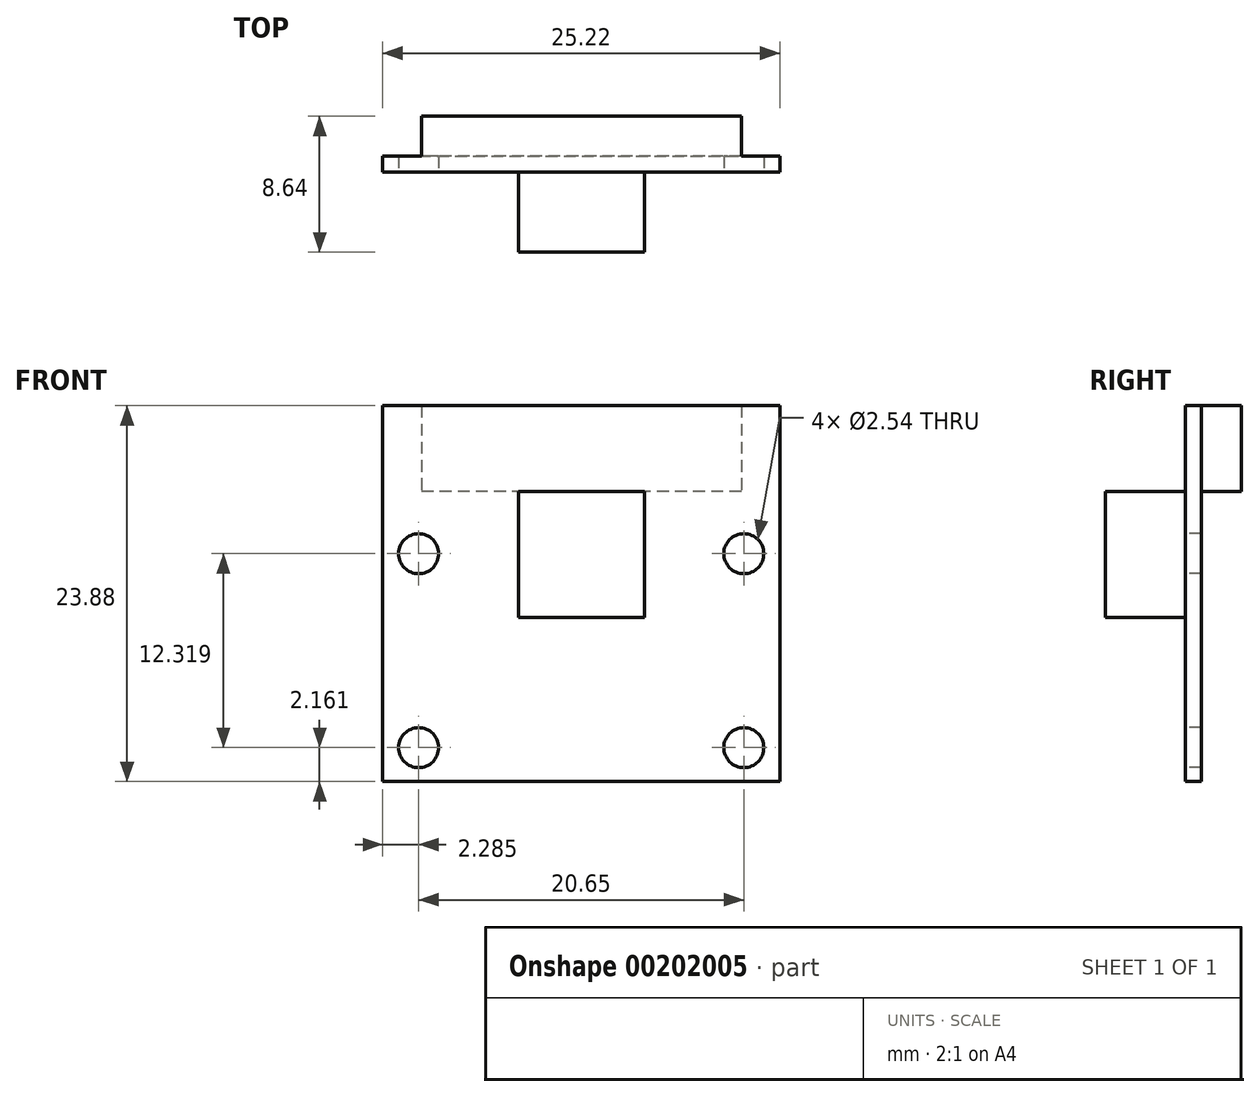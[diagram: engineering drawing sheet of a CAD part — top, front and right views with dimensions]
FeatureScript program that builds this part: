
annotation { "Feature Type Name" : "Feature", "Feature Type Description" : "" }
export const myFeature = defineFeature(function(context is Context, id is Id, definition is map)
    precondition{}
    {
        {
            var Q0;
            Q0=qCreatedBy(makeId("Front.planeOp"),FACE);
            var sketch = newSketch(context, id + "F0", { "sketchPlane" : qUnion([Q0])});
            skLineSegment(sketch, "E0.bottom", {"start": v(-12.61, 11.94) * mm, "end": v(12.61, 11.94) * mm});
            skLineSegment(sketch, "E0.top", {"start": v(-12.61, -11.94) * mm, "end": v(12.61, -11.94) * mm});
            skLineSegment(sketch, "E0.left", {"start": v(-12.61, 11.94) * mm, "end": v(-12.61, -11.94) * mm});
            skLineSegment(sketch, "E0.right", {"start": v(12.61, 11.94) * mm, "end": v(12.61, -11.94) * mm});
            skPoint(sketch, "E0.middle", {"position": v(0, 0) * mm});
            skCircle(sketch, "E1", {"center": v(10.33, -9.78) * mm, "radius": 1.27 * mm});
            skLineSegment(sketch, "E2", {"start": v(0, 11.94) * mm, "end": v(0, -11.94) * mm, "construction": true});
            skCircle(sketch, "E3", {"center": v(10.33, 2.54) * mm, "radius": 1.27 * mm});
            skCircle(sketch, "E4.MirrorC", {"center": v(-10.33, 2.54) * mm, "radius": 1.27 * mm});
            skCircle(sketch, "E5.MirrorC", {"center": v(-10.33, -9.78) * mm, "radius": 1.27 * mm});
            skSolve(sketch);
        }
        {
            var Q0;
            Q0=makeQuery(id+"F0.imprint","IMPRINT",FACE,{"disambiguationData":[TD([[makeQuery(id+"F0.imprint","IMPRINT",EDGE,{"derivedFrom":sQuery(id+"F0.wireOp",EDGE,"E0.bottom")}),-1.0]])]});
            extrude(context, id + "F1", {"entities" : qUnion([Q0]), "oppositeDirection" : true, "depth" : 1.02 * mm});
        }
        {
            var Q0;
            Q0=makeQuery(id+"F1.opExtrude","CAP_FACE",FACE,{"disambiguationData":[OSD([sQuery(id+"F0.wireOp",EDGE,"E0.bottom"),sQuery(id+"F0.wireOp",EDGE,"E0.top"),sQuery(id+"F0.wireOp",EDGE,"E0.left"),sQuery(id+"F0.wireOp",EDGE,"E0.right")])],"isStart":true});
            var sketch = newSketch(context, id + "F2", { "sketchPlane" : qUnion([Q0])});
            skLineSegment(sketch, "E6.bottom", {"start": v(-4, 6.48) * mm, "end": v(4, 6.48) * mm});
            skLineSegment(sketch, "E6.top", {"start": v(-4, -1.52) * mm, "end": v(4, -1.52) * mm});
            skLineSegment(sketch, "E6.left", {"start": v(-4, 6.48) * mm, "end": v(-4, -1.52) * mm});
            skLineSegment(sketch, "E6.right", {"start": v(4, 6.48) * mm, "end": v(4, -1.52) * mm});
            skPoint(sketch, "E6.middle", {"position": v(0, 2.48) * mm});
            skSolve(sketch);
        }
        {
            var Q0;
            Q0=makeQuery(id+"F2.imprint","IMPRINT",FACE,{"disambiguationData":[TD([[makeQuery(id+"F2.imprint","IMPRINT",EDGE,{"derivedFrom":sQuery(id+"F2.wireOp",EDGE,"E6.bottom")}),-1.0]])]});
            extrude(context, id + "F3", {"entities" : qUnion([Q0]), "operationType" : NewBodyOperationType.ADD, "depth" : 5.08 * mm});
        }
        {
            var Q0;
            Q0=makeQuery(id+"F1.opExtrude","CAP_FACE",FACE,{"disambiguationData":[OSD([sQuery(id+"F0.wireOp",EDGE,"E0.bottom"),sQuery(id+"F0.wireOp",EDGE,"E0.top"),sQuery(id+"F0.wireOp",EDGE,"E0.left"),sQuery(id+"F0.wireOp",EDGE,"E0.right")])],"isStart":false});
            var sketch = newSketch(context, id + "F4", { "sketchPlane" : qUnion([Q0])});
            skLineSegment(sketch, "E7.bottom", {"start": v(-10.16, 11.94) * mm, "end": v(10.16, 11.94) * mm});
            skLineSegment(sketch, "E7.top", {"start": v(-10.16, 6.48) * mm, "end": v(10.16, 6.48) * mm});
            skLineSegment(sketch, "E7.left", {"start": v(-10.16, 11.94) * mm, "end": v(-10.16, 6.48) * mm});
            skLineSegment(sketch, "E7.right", {"start": v(10.16, 11.94) * mm, "end": v(10.16, 6.48) * mm});
            skPoint(sketch, "E7.middle", {"position": v(0, 9.2) * mm});
            skSolve(sketch);
        }
        {
            var Q0;
            Q0=makeQuery(id+"F4.imprint","IMPRINT",FACE,{"disambiguationData":[TD([[makeQuery(id+"F4.imprint","IMPRINT",EDGE,{"derivedFrom":sQuery(id+"F4.wireOp",EDGE,"E7.bottom")}),1.0]])]});
            extrude(context, id + "F5", {"entities" : qUnion([Q0]), "operationType" : NewBodyOperationType.ADD, "depth" : 2.54 * mm});
        }
    });
